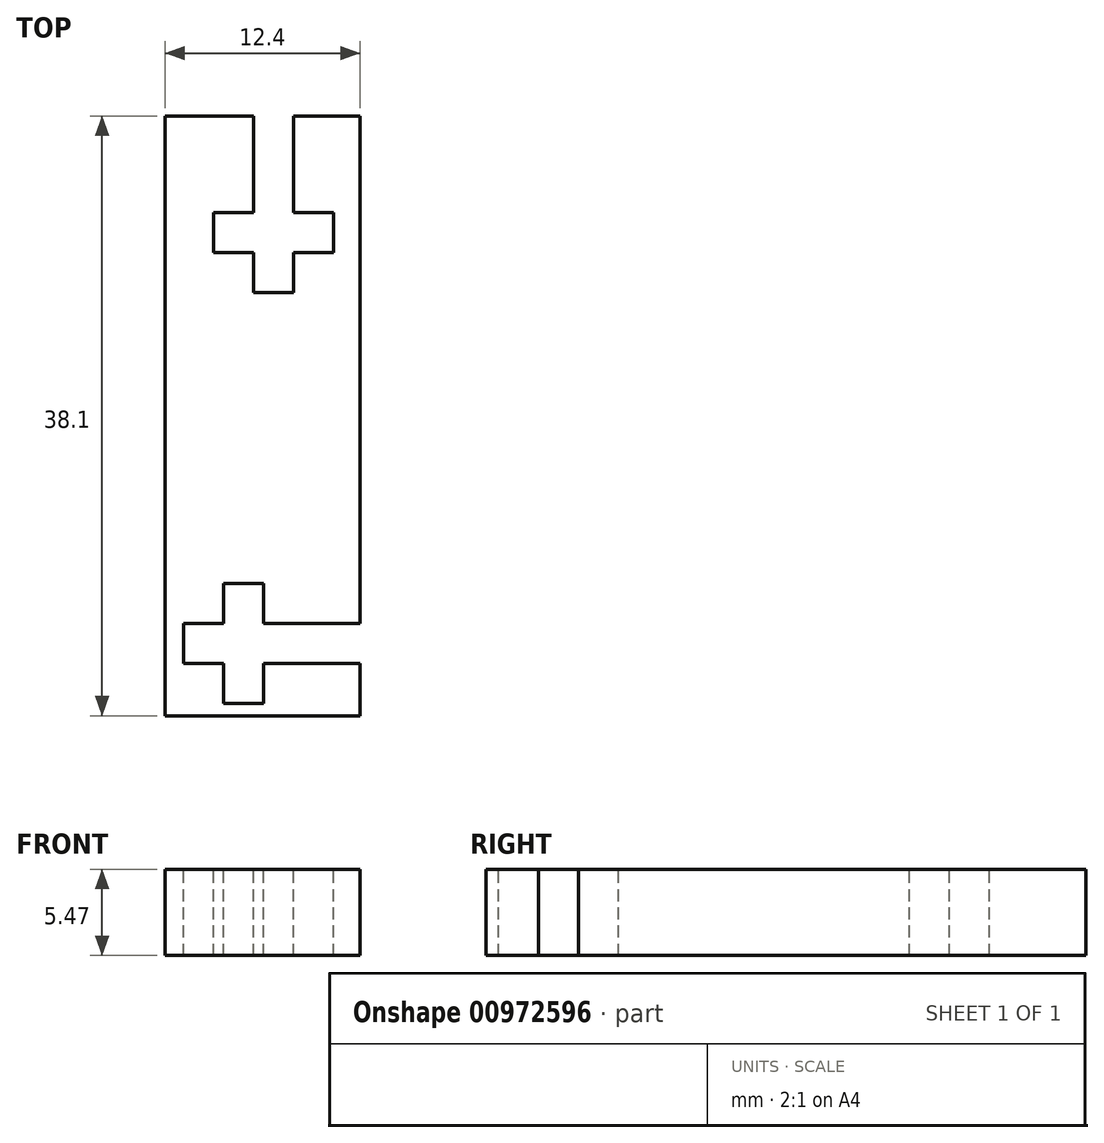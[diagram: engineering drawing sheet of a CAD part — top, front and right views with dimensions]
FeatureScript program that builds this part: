
annotation { "Feature Type Name" : "Feature", "Feature Type Description" : "" }
export const myFeature = defineFeature(function(context is Context, id is Id, definition is map)
    precondition{}
    {
        {
            var Q0;
            Q0=qCreatedBy(makeId("Front.planeOp"),FACE);
            var sketch = newSketch(context, id + "F0", { "sketchPlane" : qUnion([Q0])});
            skLineSegment(sketch, "E0", {"start": v(12.4, 5.47) * mm, "end": v(0, 5.47) * mm});
            skLineSegment(sketch, "E1", {"start": v(0, 0) * mm, "end": v(12.4, 0) * mm});
            skLineSegment(sketch, "E2", {"start": v(0, 0) * mm, "end": v(0, 5.47) * mm});
            skLineSegment(sketch, "E3", {"start": v(12.4, 5.47) * mm, "end": v(12.4, 0) * mm});
            skSolve(sketch);
        }
        {
            var Q0;
            Q0 = qSketchRegion(id + "F0", true);
            extrude(context, id + "F1", {"entities" : qUnion([Q0]), "depth" : 38.1 * mm, "offsetDistance" : 25.4 * mm});
        }
        {
            var Q0;
            Q0=makeQuery(id+"F1.opExtrude","SWEPT_FACE",FACE,{"disambiguationData":[OSD([sQuery(id+"F0.wireOp",EDGE,"E0")])]});
            var sketch = newSketch(context, id + "F2", { "sketchPlane" : qUnion([Q0])});
            skLineSegment(sketch, "E4", {"start": v(5.64, 0) * mm, "end": v(5.64, -6.15) * mm});
            skLineSegment(sketch, "E5", {"start": v(5.64, -6.15) * mm, "end": v(3.1, -6.15) * mm});
            skLineSegment(sketch, "E6", {"start": v(8.18, 0) * mm, "end": v(8.18, -6.15) * mm});
            skLineSegment(sketch, "E7", {"start": v(8.18, -6.15) * mm, "end": v(10.72, -6.15) * mm});
            skLineSegment(sketch, "E8", {"start": v(3.1, -6.15) * mm, "end": v(3.1, -8.69) * mm});
            skLineSegment(sketch, "E9", {"start": v(3.1, -8.69) * mm, "end": v(5.64, -8.69) * mm});
            skLineSegment(sketch, "E10", {"start": v(10.72, -6.15) * mm, "end": v(10.72, -8.69) * mm});
            skLineSegment(sketch, "E11", {"start": v(10.72, -8.69) * mm, "end": v(8.18, -8.69) * mm});
            skLineSegment(sketch, "E12", {"start": v(8.18, -8.69) * mm, "end": v(8.18, -11.23) * mm});
            skLineSegment(sketch, "E13", {"start": v(8.18, -11.23) * mm, "end": v(5.64, -11.23) * mm});
            skLineSegment(sketch, "E14", {"start": v(5.64, -8.69) * mm, "end": v(5.64, -11.23) * mm});
            skLineSegment(sketch, "E15", {"start": v(12.4, -32.23) * mm, "end": v(6.25, -32.23) * mm});
            skLineSegment(sketch, "E16", {"start": v(12.4, -34.77) * mm, "end": v(6.25, -34.77) * mm});
            skLineSegment(sketch, "E17", {"start": v(6.25, -32.23) * mm, "end": v(6.25, -29.7) * mm});
            skLineSegment(sketch, "E18", {"start": v(6.25, -29.7) * mm, "end": v(3.7, -29.7) * mm});
            skLineSegment(sketch, "E19", {"start": v(3.7, -29.7) * mm, "end": v(3.7, -32.23) * mm});
            skLineSegment(sketch, "E20", {"start": v(3.7, -32.23) * mm, "end": v(1.17, -32.23) * mm});
            skLineSegment(sketch, "E21", {"start": v(1.17, -32.23) * mm, "end": v(1.17, -34.77) * mm});
            skLineSegment(sketch, "E22", {"start": v(1.17, -34.77) * mm, "end": v(3.7, -34.77) * mm});
            skLineSegment(sketch, "E23", {"start": v(3.7, -34.77) * mm, "end": v(3.7, -37.31) * mm});
            skLineSegment(sketch, "E24", {"start": v(3.7, -37.31) * mm, "end": v(6.25, -37.31) * mm});
            skLineSegment(sketch, "E25", {"start": v(6.25, -37.31) * mm, "end": v(6.25, -34.77) * mm});
            skSolve(sketch);
        }
        {
            var Q0;
            Q0 = qSketchRegion(id + "F2", true);
            var Q1;
            {var subQ0=sQuery(id+"F2.wireOp",EDGE,"E4");Q1=makeQuery(id+"F2.imprint","IMPRINT",FACE,{"disambiguationData":[TD([[makeQuery(id+"F2.imprint","IMPRINT",EDGE,{"derivedFrom":subQ0}),1.0]])]});}
            extrude(context, id + "F3", {"entities" : qUnion([Q0, Q1]), "operationType" : NewBodyOperationType.REMOVE, "oppositeDirection" : true, "depth" : 25.4 * mm, "offsetDistance" : 25.4 * mm});
        }
        {
            var Q0;
            {var subQ0=sQuery(id+"F2.wireOp",EDGE,"E15");Q0=makeQuery(id+"F2.imprint","IMPRINT",FACE,{"disambiguationData":[TD([[makeQuery(id+"F2.imprint","IMPRINT",EDGE,{"derivedFrom":subQ0}),1.0]])]});}
            extrude(context, id + "F4", {"entities" : qUnion([Q0]), "operationType" : NewBodyOperationType.REMOVE, "oppositeDirection" : true, "depth" : 25.4 * mm, "offsetDistance" : 25.4 * mm});
        }
    });
